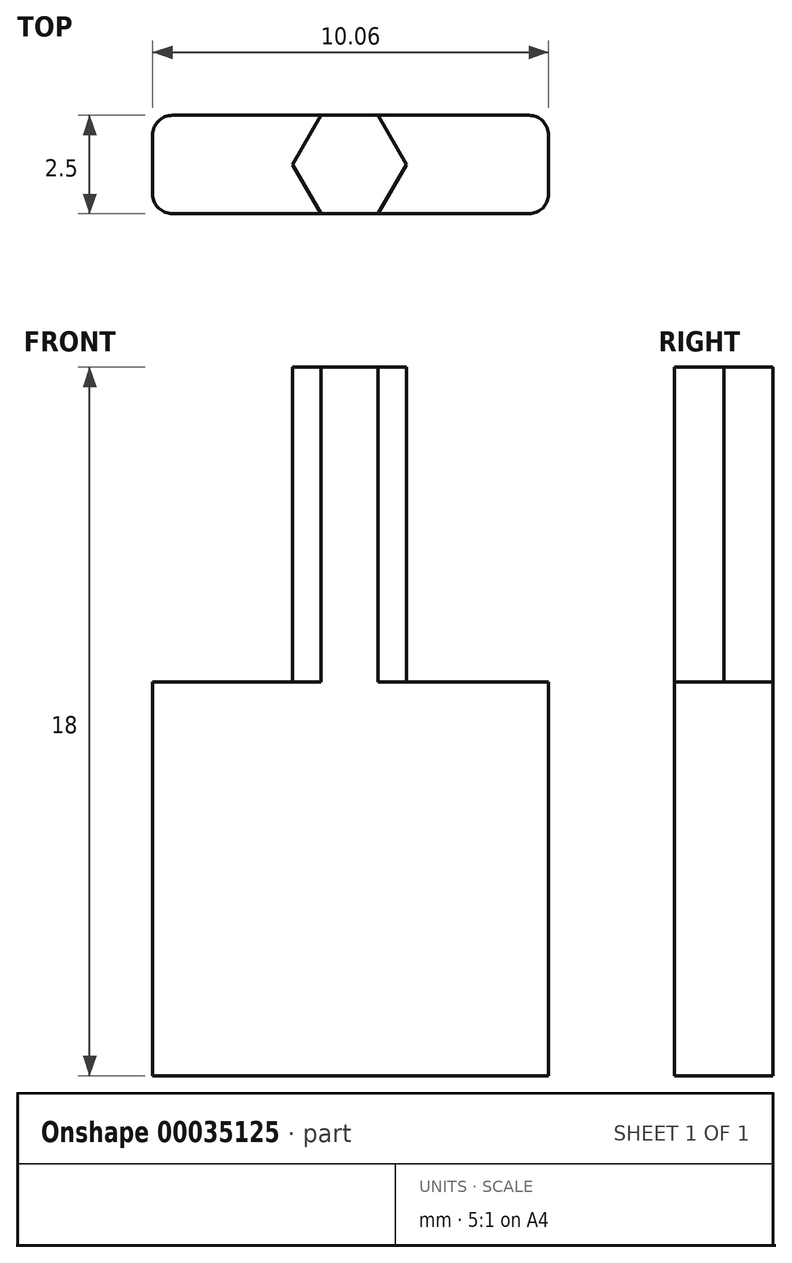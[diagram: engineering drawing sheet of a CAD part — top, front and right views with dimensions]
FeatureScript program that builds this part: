
annotation { "Feature Type Name" : "Feature", "Feature Type Description" : "" }
export const myFeature = defineFeature(function(context is Context, id is Id, definition is map)
    precondition{}
    {
        {
            var Q0;
            Q0=qCreatedBy(makeId("Top.planeOp"),FACE);
            var sketch = newSketch(context, id + "F0", { "sketchPlane" : qUnion([Q0])});
            skCircle(sketch, "E0.cCircle", {"center": v(0, 0) * mm, "radius": 1.25 * mm, "construction": true});
            skLineSegment(sketch, "E0.0", {"start": v(-0.72, 1.25) * mm, "end": v(0.72, 1.25) * mm});
            skLineSegment(sketch, "E0.1", {"start": v(0.72, 1.25) * mm, "end": v(1.44, 0) * mm});
            skLineSegment(sketch, "E0.2", {"start": v(1.44, 0) * mm, "end": v(0.72, -1.25) * mm});
            skLineSegment(sketch, "E0.3", {"start": v(0.72, -1.25) * mm, "end": v(-0.72, -1.25) * mm});
            skLineSegment(sketch, "E0.4", {"start": v(-0.72, -1.25) * mm, "end": v(-1.44, 0) * mm});
            skLineSegment(sketch, "E0.5", {"start": v(-1.44, 0) * mm, "end": v(-0.72, 1.25) * mm});
            skPoint(sketch, "E0.0.midPoint", {"position": v(0, 1.25) * mm});
            skSolve(sketch);
        }
        {
            var Q0;
            Q0 = qSketchRegion(id + "F0", true);
            extrude(context, id + "F1", {"entities" : qUnion([Q0]), "depth" : 8 * mm});
        }
        {
            var Q0;
            Q0=qCreatedBy(makeId("Front.planeOp"),FACE);
            var sketch = newSketch(context, id + "F2", { "sketchPlane" : qUnion([Q0])});
            skLineSegment(sketch, "E1.bottom", {"start": v(-5, 0) * mm, "end": v(5.06, 0) * mm});
            skLineSegment(sketch, "E1.top", {"start": v(-5, -10) * mm, "end": v(5.06, -10) * mm});
            skLineSegment(sketch, "E1.left", {"start": v(-5, 0) * mm, "end": v(-5, -10) * mm});
            skLineSegment(sketch, "E1.right", {"start": v(5.06, 0) * mm, "end": v(5.06, -10) * mm});
            skSolve(sketch);
        }
        {
            var Q0;
            Q0 = qSketchRegion(id + "F2", true);
            extrude(context, id + "F3", {"entities" : qUnion([Q0]), "operationType" : NewBodyOperationType.ADD, "depth" : 1.25 * mm, "hasSecondDirection" : true, "secondDirectionOppositeDirection" : true, "secondDirectionDepth" : 1.25 * mm});
        }
        {
            var Q0;
            Q0=makeQuery(id+"F3.opExtrude","CAP_EDGE",EDGE,{"disambiguationData":[OSD([sQuery(id+"F2.wireOp",EDGE,"E1.right")])],"isStart":false});
            var Q1;
            Q1=makeQuery(id+"F3.opExtrude","CAP_EDGE",EDGE,{"disambiguationData":[OSD([sQuery(id+"F2.wireOp",EDGE,"E1.right")])],"isStart":true});
            var Q2;
            Q2=makeQuery(id+"F3.opExtrude","CAP_EDGE",EDGE,{"disambiguationData":[OSD([sQuery(id+"F2.wireOp",EDGE,"E1.left")])],"isStart":false});
            var Q3;
            Q3=makeQuery(id+"F3.opExtrude","CAP_EDGE",EDGE,{"disambiguationData":[OSD([sQuery(id+"F2.wireOp",EDGE,"E1.left")])],"isStart":true});
            fillet(context, id + "F4", {"entities" : qUnion([Q0, Q1, Q2, Q3]), "radius" : 0.5 * mm, "tangentPropagation" : true, "allowEdgeOverflow" : false});
        }
    });
